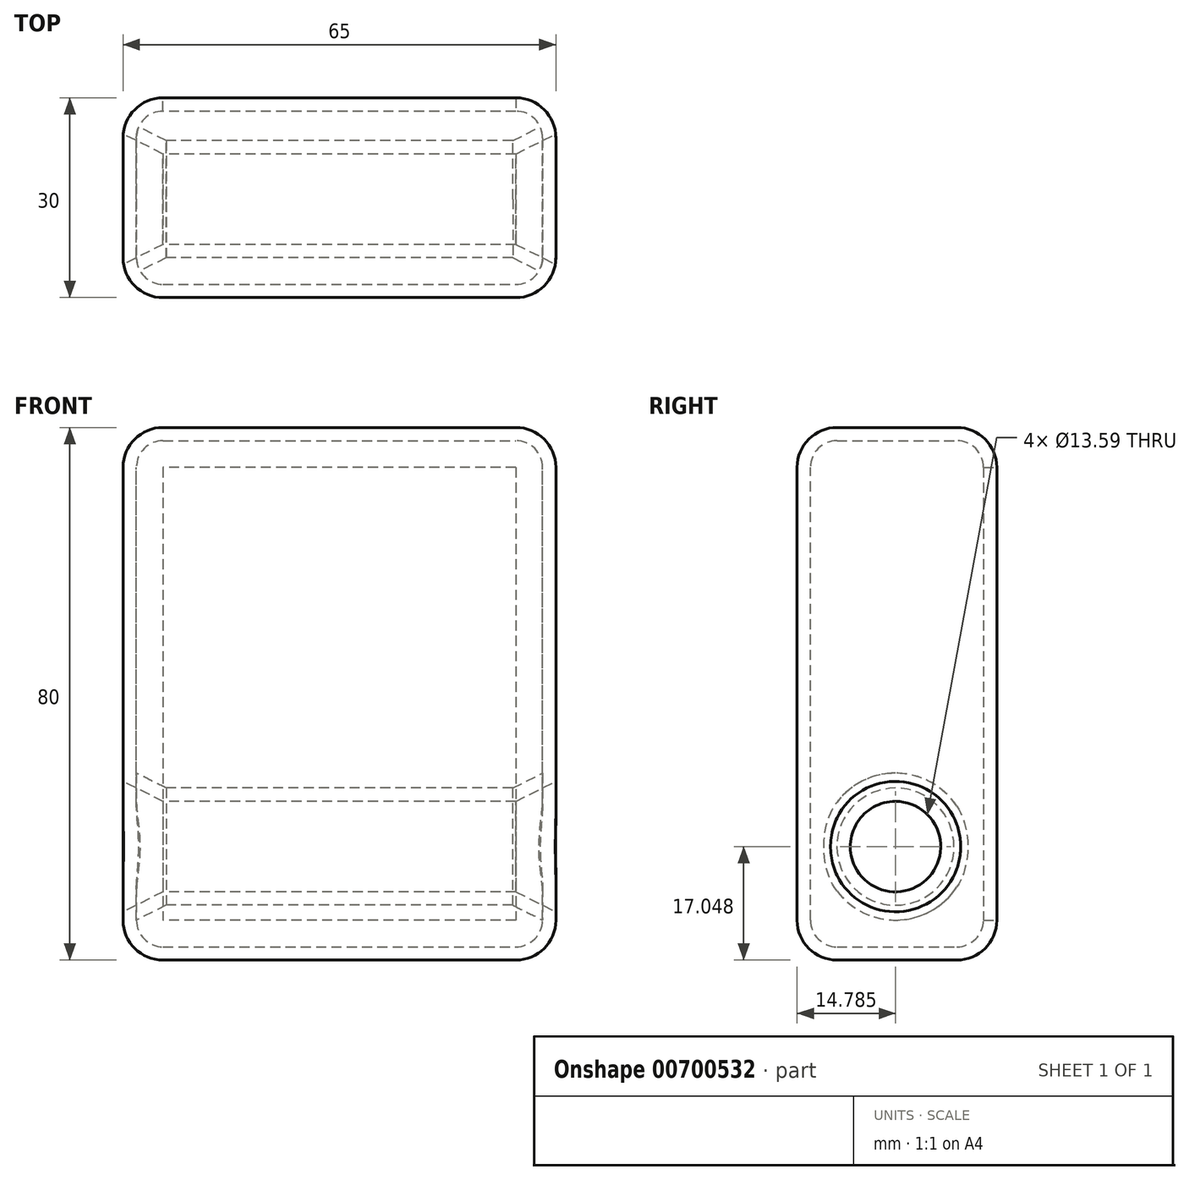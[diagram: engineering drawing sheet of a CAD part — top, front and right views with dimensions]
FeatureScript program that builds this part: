
annotation { "Feature Type Name" : "Feature", "Feature Type Description" : "" }
export const myFeature = defineFeature(function(context is Context, id is Id, definition is map)
    precondition{}
    {
        {
            var Q0;
            Q0=qCreatedBy(makeId("Front.planeOp"),FACE);
            var sketch = newSketch(context, id + "F0", { "sketchPlane" : qUnion([Q0])});
            skLineSegment(sketch, "E0.bottom", {"start": v(65, 80) * mm, "end": v(0, 80) * mm});
            skLineSegment(sketch, "E0.top", {"start": v(65, 0) * mm, "end": v(0, 0) * mm});
            skLineSegment(sketch, "E0.left", {"start": v(65, 80) * mm, "end": v(65, 0) * mm});
            skLineSegment(sketch, "E0.right", {"start": v(0, 80) * mm, "end": v(0, 0) * mm});
            skSolve(sketch);
        }
        {
            var Q0;
            Q0 = qSketchRegion(id + "F0", true);
            extrude(context, id + "F1", {"entities" : qUnion([Q0]), "oppositeDirection" : true, "depth" : 30 * mm, "offsetDistance" : 25 * mm});
        }
        {
            var Q0;
            Q0=qCreatedBy(makeId("Right.planeOp"),FACE);
            var sketch = newSketch(context, id + "F2", { "sketchPlane" : qUnion([Q0])});
            skCircle(sketch, "E1", {"center": v(14.78, 17.05) * mm, "radius": 6.8 * mm});
            skSolve(sketch);
        }
        {
            var Q0;
            Q0 = qSketchRegion(id + "F2", true);
            extrude(context, id + "F3", {"entities" : qUnion([Q0]), "operationType" : NewBodyOperationType.REMOVE, "endBound" : BoundingType.UP_TO_NEXT, "depth" : 25 * mm, "offsetDistance" : 25 * mm});
        }
        {
            var Q0;
            Q0=makeQuery(id+"F1.opExtrude","SWEPT_EDGE",EDGE,{"disambiguationData":[OSD([sQuery(id+"F0.wireOp",EDGE,"E0.bottom"),sQuery(id+"F0.wireOp",EDGE,"E0.left")])]});
            var Q1;
            Q1=makeQuery(id+"F1.opExtrude","CAP_EDGE",EDGE,{"disambiguationData":[OSD([sQuery(id+"F0.wireOp",EDGE,"E0.bottom")])],"isStart":true});
            var Q2;
            Q2=makeQuery(id+"F1.opExtrude","CAP_EDGE",EDGE,{"disambiguationData":[OSD([sQuery(id+"F0.wireOp",EDGE,"E0.left")])],"isStart":true});
            var Q3;
            Q3=makeQuery(id+"F1.opExtrude","CAP_EDGE",EDGE,{"disambiguationData":[OSD([sQuery(id+"F0.wireOp",EDGE,"E0.top")])],"isStart":true});
            var Q4;
            Q4=makeQuery(id+"F1.opExtrude","CAP_EDGE",EDGE,{"disambiguationData":[OSD([sQuery(id+"F0.wireOp",EDGE,"E0.right")])],"isStart":true});
            var Q5;
            Q5=makeQuery(id+"F1.opExtrude","SWEPT_EDGE",EDGE,{"disambiguationData":[OSD([sQuery(id+"F0.wireOp",EDGE,"E0.top"),sQuery(id+"F0.wireOp",EDGE,"E0.right")])]});
            var Q6;
            Q6=makeQuery(id+"F1.opExtrude","CAP_EDGE",EDGE,{"disambiguationData":[OSD([sQuery(id+"F0.wireOp",EDGE,"E0.right")])],"isStart":false});
            var Q7;
            Q7=makeQuery(id+"F1.opExtrude","CAP_EDGE",EDGE,{"disambiguationData":[OSD([sQuery(id+"F0.wireOp",EDGE,"E0.top")])],"isStart":false});
            var Q8;
            Q8=makeQuery(id+"F1.opExtrude","SWEPT_EDGE",EDGE,{"disambiguationData":[OSD([sQuery(id+"F0.wireOp",EDGE,"E0.top"),sQuery(id+"F0.wireOp",EDGE,"E0.left")])]});
            var Q9;
            Q9=makeQuery(id+"F1.opExtrude","SWEPT_EDGE",EDGE,{"disambiguationData":[OSD([sQuery(id+"F0.wireOp",EDGE,"E0.bottom"),sQuery(id+"F0.wireOp",EDGE,"E0.right")])]});
            var Q10;
            Q10=makeQuery(id+"F1.opExtrude","CAP_EDGE",EDGE,{"disambiguationData":[OSD([sQuery(id+"F0.wireOp",EDGE,"E0.left")])],"isStart":false});
            var Q11;
            Q11=makeQuery(id+"F1.opExtrude","CAP_FACE",FACE,{"disambiguationData":[OSD([sQuery(id+"F0.wireOp",EDGE,"E0.bottom"),sQuery(id+"F0.wireOp",EDGE,"E0.top"),sQuery(id+"F0.wireOp",EDGE,"E0.left"),sQuery(id+"F0.wireOp",EDGE,"E0.right")])],"isStart":false});
            fillet(context, id + "F4", {"entities" : qUnion([Q0, Q1, Q2, Q3, Q4, Q5, Q6, Q7, Q8, Q9, Q10, Q11]), "radius" : 6 * mm, "tangentPropagation" : true, "allowEdgeOverflow" : false});
        }
        {
            var Q0;
            Q0=makeQuery(id+"F3.boolean.opBoolean","COPY",EDGE,{"derivedFrom":makeQuery(id+"F3.opExtrude","TWEAK_EDGE",EDGE,{"derivedFrom":[makeQuery(id+"F1.opExtrude","SWEPT_FACE",FACE,{"disambiguationData":[OSD([sQuery(id+"F0.wireOp",EDGE,"E0.left")])]}),makeQuery(id+"F2.imprint","IMPRINT",EDGE,{"derivedFrom":sQuery(id+"F2.wireOp",EDGE,"E1")})]})});
            var Q1;
            Q1=makeQuery(id+"F3.boolean.opBoolean","COPY",FACE,{"derivedFrom":makeQuery(id+"F3.opExtrude","SWEPT_FACE",FACE,{"disambiguationData":[OSD([sQuery(id+"F2.wireOp",EDGE,"E1")])]})});
            chamfer(context, id + "F5", {"entities" : qUnion([Q0, Q1]), "chamferType" : ChamferType.TWO_OFFSETS, "width1" : 3 * mm, "oppositeDirection" : false, "width2" : 6 * mm, "tangentPropagation" : true});
        }
        {
            var Q0;
            Q0=makeQuery(id+"F1.opExtrude","CAP_FACE",FACE,{"disambiguationData":[OSD([sQuery(id+"F0.wireOp",EDGE,"E0.bottom"),sQuery(id+"F0.wireOp",EDGE,"E0.top"),sQuery(id+"F0.wireOp",EDGE,"E0.left"),sQuery(id+"F0.wireOp",EDGE,"E0.right")])],"isStart":false});
            shell(context, id + "F6", {"entities" : qUnion([Q0]), "thickness" : 2 * mm});
        }
    });
